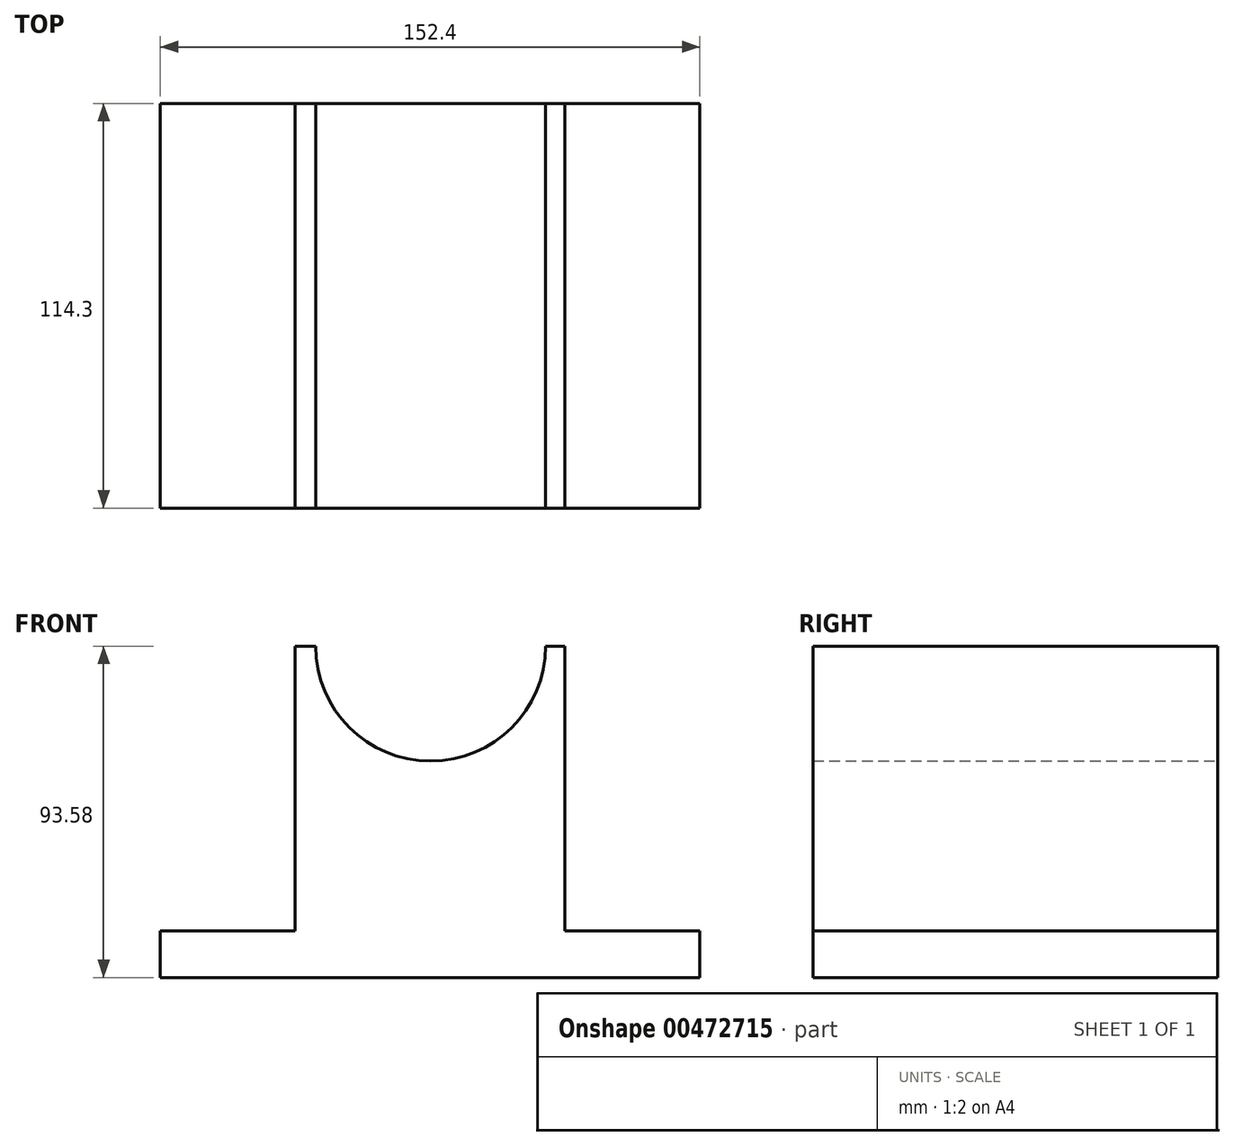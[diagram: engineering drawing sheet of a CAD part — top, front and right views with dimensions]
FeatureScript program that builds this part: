
annotation { "Feature Type Name" : "Feature", "Feature Type Description" : "" }
export const myFeature = defineFeature(function(context is Context, id is Id, definition is map)
    precondition{}
    {
        {
            var Q0;
            Q0=qCreatedBy(makeId("Front.planeOp"),FACE);
            var sketch = newSketch(context, id + "F0", { "sketchPlane" : qUnion([Q0])});
            skLineSegment(sketch, "E0.bottom", {"start": v(-38.1, 46.79) * mm, "end": v(-32.3, 46.79) * mm});
            skLineSegment(sketch, "E0.top", {"start": v(-38.1, -46.79) * mm, "end": v(38.1, -46.79) * mm});
            skLineSegment(sketch, "E0.left", {"start": v(-38.1, 46.79) * mm, "end": v(-38.1, -33.68) * mm});
            skLineSegment(sketch, "E0.right", {"start": v(38.1, 46.79) * mm, "end": v(38.1, -33.68) * mm});
            skPoint(sketch, "E0.middle", {"position": v(0, 0) * mm});
            skLineSegment(sketch, "E1.bottom", {"start": v(-38.1, -46.79) * mm, "end": v(-76.2, -46.79) * mm});
            skLineSegment(sketch, "E1.top", {"start": v(-38.1, -33.68) * mm, "end": v(-76.2, -33.68) * mm});
            skLineSegment(sketch, "E1.right", {"start": v(-76.2, -46.79) * mm, "end": v(-76.2, -33.68) * mm});
            skLineSegment(sketch, "E2.MirrorCS", {"start": v(38.1, -33.68) * mm, "end": v(76.2, -33.68) * mm});
            skLineSegment(sketch, "E3.MirrorCS", {"start": v(38.1, -46.79) * mm, "end": v(76.2, -46.79) * mm});
            skLineSegment(sketch, "E4.MirrorCS", {"start": v(76.2, -46.79) * mm, "end": v(76.2, -33.68) * mm});
            skArc(sketch, "E5", {"start": v(-32.3, 46.79) * mm, "mid": v(0.15, 14.33) * mm, "end": v(32.61, 46.79) * mm});
            skLineSegment(sketch, "E6.trimOffspring", {"start": v(32.61, 46.79) * mm, "end": v(38.1, 46.79) * mm});
            skPoint(sketch, "E7.MirrorCS.end.orphan", {"position": v(38.1, -33.68) * mm});
            skPoint(sketch, "E7.MirrorCS.start.orphan", {"position": v(38.1, -46.79) * mm});
            skSolve(sketch);
        }
        {
            var Q0;
            Q0=makeQuery(id+"F0.imprint","IMPRINT",FACE,{"disambiguationData":[TD([[makeQuery(id+"F0.imprint","IMPRINT",EDGE,{"derivedFrom":sQuery(id+"F0.wireOp",EDGE,"E1.bottom")}),-1.0]])]});
            var Q1;
            Q1=makeQuery(id+"F0.imprint","IMPRINT",FACE,{"disambiguationData":[TD([[makeQuery(id+"F0.imprint","IMPRINT",EDGE,{"derivedFrom":sQuery(id+"F0.wireOp",EDGE,"E7.MirrorCS")}),-1.0]])]});
            extrude(context, id + "F1", {"entities" : qUnion([Q0, Q1]), "depth" : 114.3 * mm});
        }
        {
            var Q0;
            Q0=makeQuery(id+"F0.imprint","IMPRINT",FACE,{"disambiguationData":[TD([[makeQuery(id+"F0.imprint","IMPRINT",EDGE,{"derivedFrom":sQuery(id+"F0.wireOp",EDGE,"E0.bottom")}),-1.0]])]});
            extrude(context, id + "F2", {"entities" : qUnion([Q0]), "depth" : 114.3 * mm});
        }
    });
